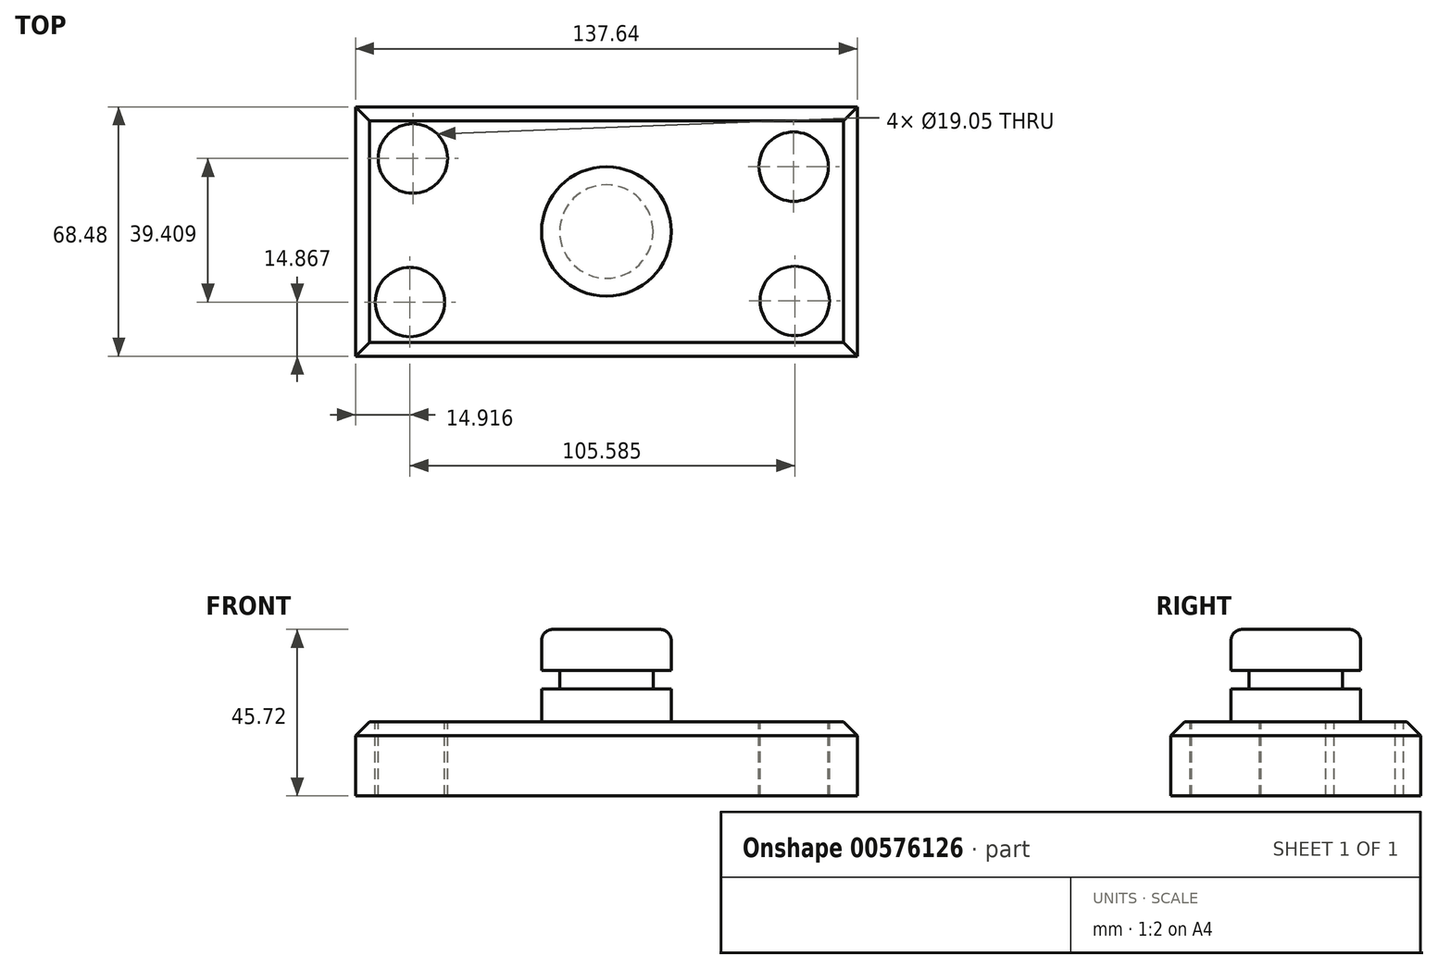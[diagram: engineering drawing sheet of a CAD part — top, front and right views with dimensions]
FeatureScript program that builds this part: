
annotation { "Feature Type Name" : "Feature", "Feature Type Description" : "" }
export const myFeature = defineFeature(function(context is Context, id is Id, definition is map)
    precondition{}
    {
        {
            var Q0;
            Q0=qCreatedBy(makeId("Top.planeOp"),FACE);
            var sketch = newSketch(context, id + "F0", { "sketchPlane" : qUnion([Q0])});
            skLineSegment(sketch, "E0.bottom", {"start": v(68.82, -34.24) * mm, "end": v(-68.82, -34.24) * mm});
            skLineSegment(sketch, "E0.top", {"start": v(68.82, 34.24) * mm, "end": v(-68.82, 34.24) * mm});
            skLineSegment(sketch, "E0.left", {"start": v(68.82, -34.24) * mm, "end": v(68.82, 34.24) * mm});
            skLineSegment(sketch, "E0.right", {"start": v(-68.82, -34.24) * mm, "end": v(-68.82, 34.24) * mm});
            skPoint(sketch, "E0.middle", {"position": v(0, 0) * mm});
            skSolve(sketch);
        }
        {
            var Q0;
            Q0 = qSketchRegion(id + "F0", true);
            extrude(context, id + "F1", {"entities" : qUnion([Q0]), "depth" : 20.32 * mm, "offsetDistance" : 25.4 * mm});
        }
        {
            var Q0;
            Q0=makeQuery(id+"F1.opExtrude","CAP_FACE",FACE,{"disambiguationData":[OSD([sQuery(id+"F0.wireOp",EDGE,"E0.bottom"),sQuery(id+"F0.wireOp",EDGE,"E0.top"),sQuery(id+"F0.wireOp",EDGE,"E0.left"),sQuery(id+"F0.wireOp",EDGE,"E0.right")])],"isStart":false});
            var sketch = newSketch(context, id + "F2", { "sketchPlane" : qUnion([Q0])});
            skCircle(sketch, "E1", {"center": v(-53.1, 20.04) * mm, "radius": 9.53 * mm});
            skCircle(sketch, "E2", {"center": v(51.68, -19.04) * mm, "radius": 9.53 * mm});
            skCircle(sketch, "E3", {"center": v(-53.9, -19.37) * mm, "radius": 9.53 * mm});
            skCircle(sketch, "E4", {"center": v(51.4, 17.8) * mm, "radius": 9.53 * mm});
            skSolve(sketch);
        }
        {
            var Q0;
            Q0=makeQuery(id+"F2.imprint","IMPRINT",FACE,{"disambiguationData":[TD([[makeQuery(id+"F2.imprint","IMPRINT",EDGE,{"derivedFrom":sQuery(id+"F2.wireOp",EDGE,"E4")}),1.0]])]});
            var Q1;
            Q1=makeQuery(id+"F2.imprint","IMPRINT",FACE,{"disambiguationData":[TD([[makeQuery(id+"F2.imprint","IMPRINT",EDGE,{"derivedFrom":sQuery(id+"F2.wireOp",EDGE,"E1")}),1.0]])]});
            var Q2;
            Q2=makeQuery(id+"F2.imprint","IMPRINT",FACE,{"disambiguationData":[TD([[makeQuery(id+"F2.imprint","IMPRINT",EDGE,{"derivedFrom":sQuery(id+"F2.wireOp",EDGE,"E3")}),1.0]])]});
            var Q3;
            Q3=makeQuery(id+"F2.imprint","IMPRINT",FACE,{"disambiguationData":[TD([[makeQuery(id+"F2.imprint","IMPRINT",EDGE,{"derivedFrom":sQuery(id+"F2.wireOp",EDGE,"E2")}),1.0]])]});
            extrude(context, id + "F3", {"entities" : qUnion([Q0, Q1, Q2, Q3]), "operationType" : NewBodyOperationType.REMOVE, "oppositeDirection" : true, "depth" : 25.4 * mm, "offsetDistance" : 25.4 * mm});
        }
        {
            var Q0;
            Q0=qCreatedBy(makeId("Front.planeOp"),FACE);
            var sketch = newSketch(context, id + "F4", { "sketchPlane" : qUnion([Q0])});
            skLineSegment(sketch, "E5.bottom", {"start": v(17.78, 20.32) * mm, "end": v(0, 20.32) * mm});
            skLineSegment(sketch, "E5.top", {"start": v(17.78, 45.72) * mm, "end": v(0, 45.72) * mm});
            skLineSegment(sketch, "E5.left", {"start": v(0, 20.32) * mm, "end": v(0, 45.72) * mm});
            skLineSegment(sketch, "E5.right", {"start": v(17.78, 20.32) * mm, "end": v(17.78, 45.72) * mm});
            skSolve(sketch);
        }
        {
            var Q0;
            Q0=makeQuery(id+"F4.imprint","IMPRINT",FACE,{"disambiguationData":[TD([[makeQuery(id+"F4.imprint","IMPRINT",EDGE,{"derivedFrom":sQuery(id+"F4.wireOp",EDGE,"E5.bottom")}),-1.0]])]});
            var Q1;
            Q1=sQuery(id+"F4.wireOp",EDGE,"E5.left");
            revolve(context, id + "F5", {"operationType" : NewBodyOperationType.ADD, "entities" : qUnion([Q0]), "axis" : qUnion([Q1]), "revolveType" : RevolveType.FULL});
        }
        {
            var Q0;
            Q0=qCreatedBy(makeId("Front.planeOp"),FACE);
            var sketch = newSketch(context, id + "F6", { "sketchPlane" : qUnion([Q0])});
            skLineSegment(sketch, "E6.bottom", {"start": v(17.88, 34.45) * mm, "end": v(12.8, 34.45) * mm});
            skLineSegment(sketch, "E6.top", {"start": v(17.88, 29.37) * mm, "end": v(12.8, 29.37) * mm});
            skLineSegment(sketch, "E6.left", {"start": v(17.88, 34.45) * mm, "end": v(17.88, 29.37) * mm});
            skLineSegment(sketch, "E6.right", {"start": v(12.8, 34.45) * mm, "end": v(12.8, 29.37) * mm});
            skLineSegment(sketch, "E7", {"start": v(0, 86.72) * mm, "end": v(0, 0) * mm});
            skSolve(sketch);
        }
        {
            var Q0;
            Q0 = qSketchRegion(id + "F6", true);
            var Q1;
            Q1=sQuery(id+"F6.wireOp",EDGE,"E7");
            revolve(context, id + "F7", {"operationType" : NewBodyOperationType.REMOVE, "entities" : qUnion([Q0]), "axis" : qUnion([Q1]), "revolveType" : RevolveType.FULL});
        }
        {
            var Q0;
            Q0=makeQuery(id+"F1.opExtrude","CAP_EDGE",EDGE,{"disambiguationData":[OSD([sQuery(id+"F0.wireOp",EDGE,"E0.bottom")])],"isStart":false});
            var Q1;
            Q1=makeQuery(id+"F1.opExtrude","CAP_EDGE",EDGE,{"disambiguationData":[OSD([sQuery(id+"F0.wireOp",EDGE,"E0.top")])],"isStart":false});
            var Q2;
            Q2=makeQuery(id+"F1.opExtrude","CAP_EDGE",EDGE,{"disambiguationData":[OSD([sQuery(id+"F0.wireOp",EDGE,"E0.left")])],"isStart":false});
            var Q3;
            Q3=makeQuery(id+"F1.opExtrude","CAP_EDGE",EDGE,{"disambiguationData":[OSD([sQuery(id+"F0.wireOp",EDGE,"E0.right")])],"isStart":false});
            chamfer(context, id + "F8", {"entities" : qUnion([Q0, Q1, Q2, Q3]), "width" : 3.8 * mm, "tangentPropagation" : true});
        }
        {
            var Q0;
            Q0=makeQuery(id+"F5.opRevolve","SWEPT_EDGE",EDGE,{"disambiguationData":[OSD([sQuery(id+"F4.wireOp",EDGE,"E5.top"),sQuery(id+"F4.wireOp",EDGE,"E5.right")])]});
            var Q1;
            Q1=makeQuery(id+"F5.opRevolve","SWEPT_EDGE",EDGE,{"disambiguationData":[OSD([sQuery(id+"F4.wireOp",EDGE,"E5.bottom"),sQuery(id+"F4.wireOp",EDGE,"E5.right")])]});
            fillet(context, id + "F9", {"entities" : qUnion([Q0, Q1]), "radius" : 3.05 * mm, "tangentPropagation" : true, "allowEdgeOverflow" : false});
        }
    });
